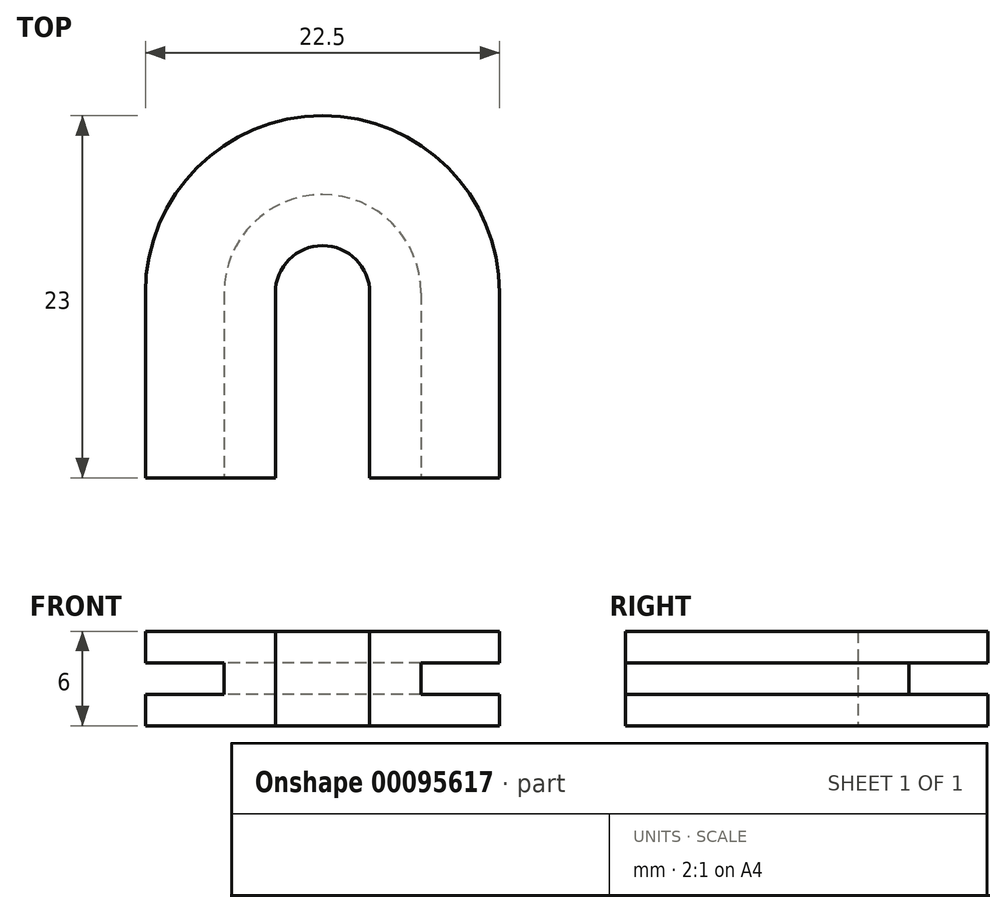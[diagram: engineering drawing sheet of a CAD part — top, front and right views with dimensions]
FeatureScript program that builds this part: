
annotation { "Feature Type Name" : "Feature", "Feature Type Description" : "" }
export const myFeature = defineFeature(function(context is Context, id is Id, definition is map)
    precondition{}
    {
        {
            var Q0;
            Q0=qCreatedBy(makeId("Top.planeOp"),FACE);
            var sketch = newSketch(context, id + "F0", { "sketchPlane" : qUnion([Q0])});
            skArc(sketch, "E0", {"start": v(6.25, 0) * mm, "mid": v(0, 6.25) * mm, "end": v(-6.25, 0) * mm});
            skLineSegment(sketch, "E1.0", {"start": v(-11.25, -11.75) * mm, "end": v(-3, -11.75) * mm});
            skLineSegment(sketch, "E1.1", {"start": v(-11.25, 0) * mm, "end": v(-11.25, -11.75) * mm});
            skArc(sketch, "E1.2", {"start": v(11.25, 0) * mm, "mid": v(0, 11.25) * mm, "end": v(-11.25, 0) * mm});
            skLineSegment(sketch, "E1.3", {"start": v(11.25, 0) * mm, "end": v(11.25, -11.75) * mm});
            skArc(sketch, "E2.0", {"start": v(3, 0) * mm, "mid": v(0, 3) * mm, "end": v(-3, 0) * mm});
            skLineSegment(sketch, "E3.trimOffspring", {"start": v(3, -11.75) * mm, "end": v(11.25, -11.75) * mm});
            skPoint(sketch, "E4.endSnap0", {"position": v(-7.12, -11.75) * mm});
            skLineSegment(sketch, "E5", {"start": v(6.25, 0) * mm, "end": v(6.25, -11.75) * mm});
            skPoint(sketch, "E4.end.orphan", {"position": v(-6.25, -11.75) * mm});
            skLineSegment(sketch, "E6", {"start": v(3, 0) * mm, "end": v(3, -11.75) * mm});
            skLineSegment(sketch, "E7", {"start": v(-3, 0) * mm, "end": v(-3, -11.75) * mm});
            skLineSegment(sketch, "E8", {"start": v(-6.25, 0) * mm, "end": v(-6.25, -11.75) * mm});
            skSolve(sketch);
        }
        {
            var Q0;
            Q0=makeQuery(id+"F0.imprint","IMPRINT",FACE,{"disambiguationData":[TD([[makeQuery(id+"F0.imprint","IMPRINT",EDGE,{"derivedFrom":sQuery(id+"F0.wireOp",EDGE,"E0")}),1.0]])]});
            extrude(context, id + "F1", {"entities" : qUnion([Q0]), "depth" : 6 * mm});
        }
        {
            var Q0;
            Q0=makeQuery(id+"F0.imprint","IMPRINT",FACE,{"disambiguationData":[TD([[makeQuery(id+"F0.imprint","IMPRINT",EDGE,{"derivedFrom":sQuery(id+"F0.wireOp",EDGE,"E0")}),-1.0]])]});
            extrude(context, id + "F2", {"entities" : qUnion([Q0]), "operationType" : NewBodyOperationType.ADD, "depth" : 6 * mm, "hasSecondDirection" : true, "secondDirectionOppositeDirection" : false, "secondDirectionDepth" : 4 * mm});
        }
        {
            var Q0;
            Q0=makeQuery(id+"F0.imprint","IMPRINT",FACE,{"disambiguationData":[TD([[makeQuery(id+"F0.imprint","IMPRINT",EDGE,{"derivedFrom":sQuery(id+"F0.wireOp",EDGE,"E0")}),-1.0]])]});
            extrude(context, id + "F3", {"entities" : qUnion([Q0]), "operationType" : NewBodyOperationType.ADD, "depth" : 2 * mm});
        }
    });
